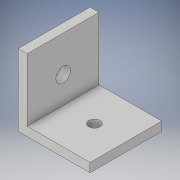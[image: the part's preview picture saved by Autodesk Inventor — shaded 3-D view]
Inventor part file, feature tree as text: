
AUTODESK INVENTOR PART (.ipt)
format: ipt  version: 2018 (Build 220112000, 112)  size: 114,176 bytes
history: native  units: in
note: dims shown in document units (in); Inventor stores cm internally (conversion verified against a paired STEP export)
features: extrude x3, sketch x3
ambient origin geometry x8: Origin, YZ Plane, XZ Plane, XY Plane, X Axis, Y Axis, Z Axis, Center Point
bodies: Solid1 (feature_tree)
feature tree (6):
  extrude  "Extrusion1"  Depth=1.0in
  extrude  "Extrusion2"  Depth=0.125in
  extrude  "Extrusion3"  Depth=1.0in
  sketch  "Sketch1"  dims[d0=0.125in d1=1.0in]
  sketch  "Sketch2"  dims[d2=1.0in d3=0.125in]
  sketch  "Sketch3"  dims[d4=1.0in d5=0.0in d6=0.5in d7=90.0deg d8=0.156in d9=1.0in d10=0.0in d11=0.2031in d12=1.0in d13=0.0in d14=0.5in]
